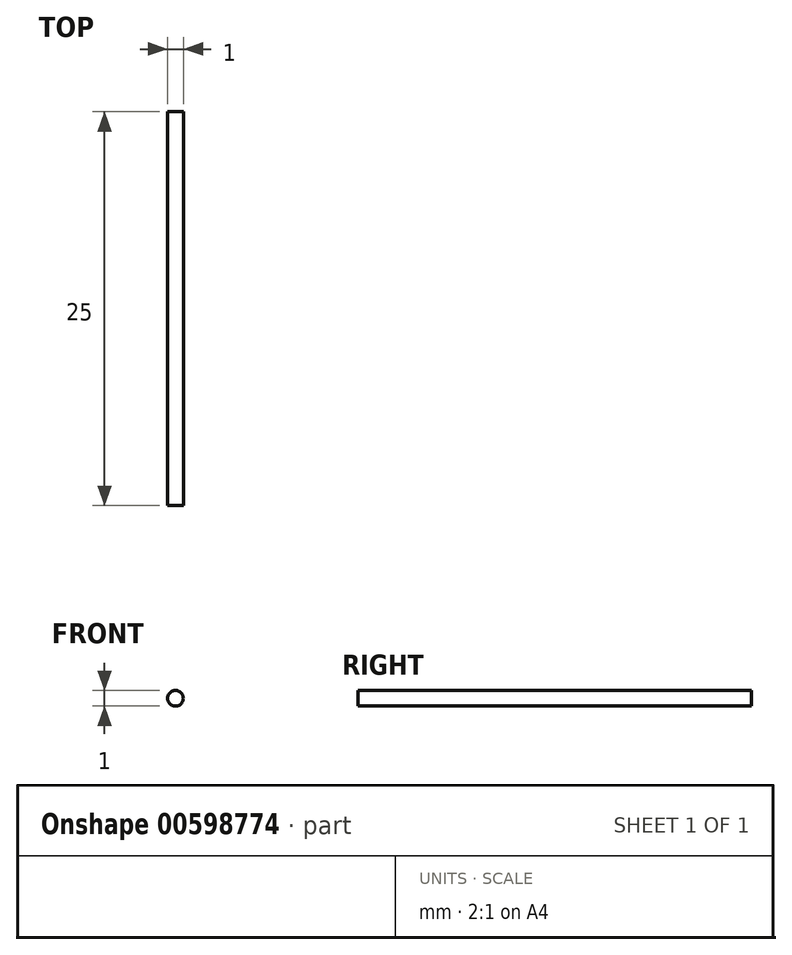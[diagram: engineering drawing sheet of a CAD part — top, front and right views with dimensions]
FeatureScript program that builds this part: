
annotation { "Feature Type Name" : "Feature", "Feature Type Description" : "" }
export const myFeature = defineFeature(function(context is Context, id is Id, definition is map)
    precondition{}
    {
        {
            var Q0;
            Q0=qCreatedBy(makeId("Front.planeOp"),FACE);
            var sketch = newSketch(context, id + "F0", { "sketchPlane" : qUnion([Q0])});
            skCircle(sketch, "E0", {"center": v(0, 0) * mm, "radius": 0.5 * mm});
            skSolve(sketch);
        }
        {
            var Q0;
            Q0 = qSketchRegion(id + "F0", true);
            extrude(context, id + "F1", {"entities" : qUnion([Q0]), "depth" : 25 * mm, "offsetDistance" : 25 * mm});
        }
    });
